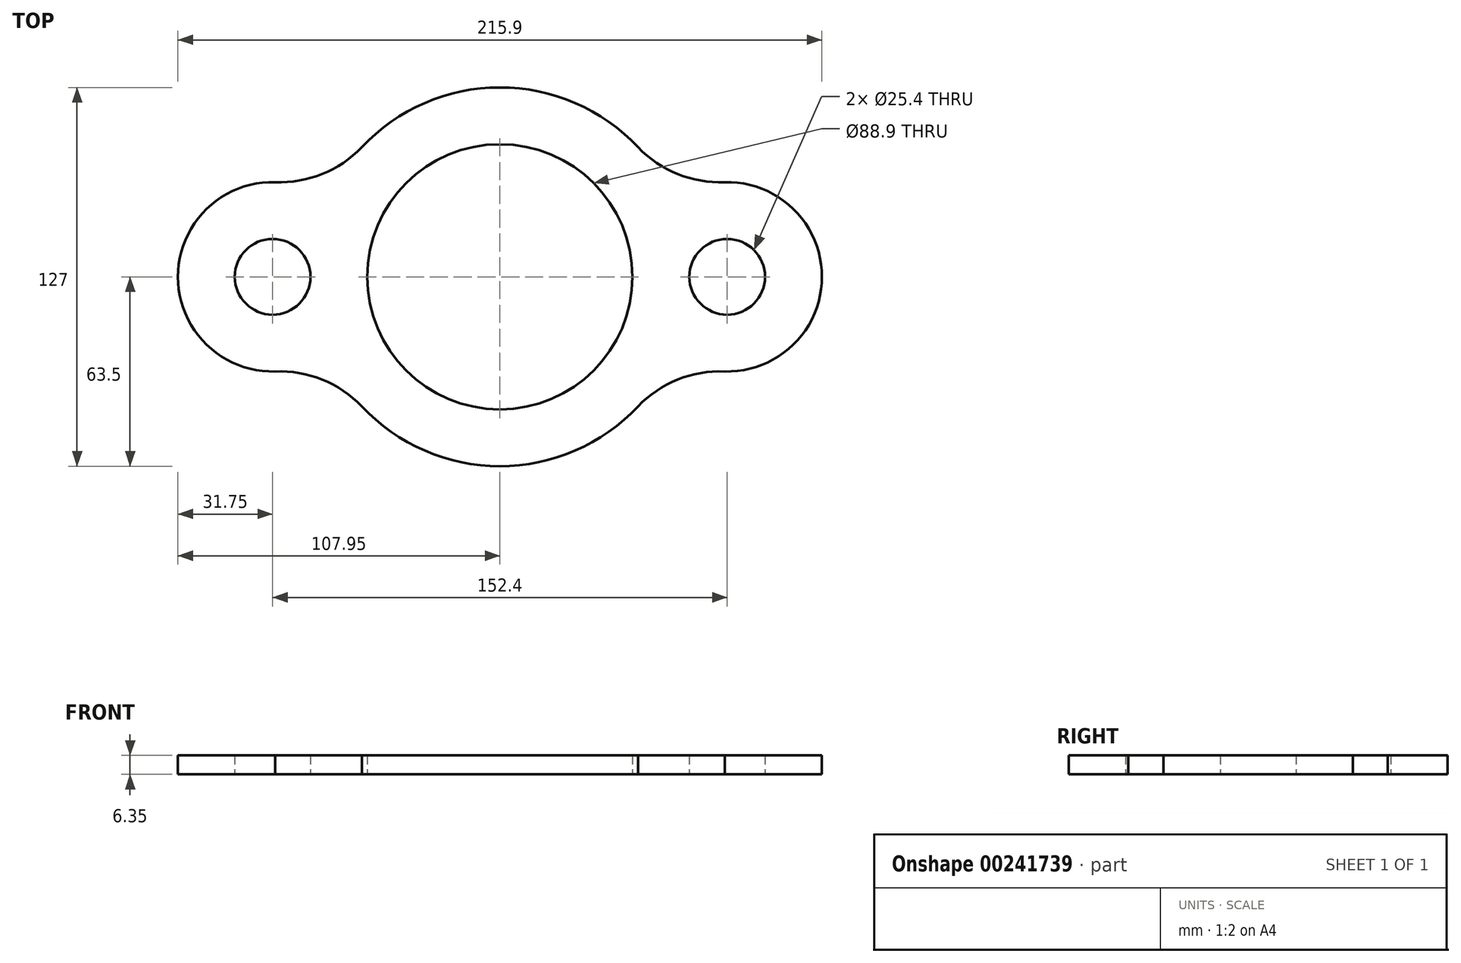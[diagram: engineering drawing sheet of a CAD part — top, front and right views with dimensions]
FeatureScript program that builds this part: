
annotation { "Feature Type Name" : "Feature", "Feature Type Description" : "" }
export const myFeature = defineFeature(function(context is Context, id is Id, definition is map)
    precondition{}
    {
        {
            var Q0;
            Q0=qCreatedBy(makeId("Top.planeOp"),FACE);
            var sketch = newSketch(context, id + "F0", { "sketchPlane" : qUnion([Q0])});
            skCircle(sketch, "E0", {"center": v(0, 0) * mm, "radius": 63.5 * mm});
            skCircle(sketch, "E1", {"center": v(-76.2, 0) * mm, "radius": 31.75 * mm});
            skCircle(sketch, "E2.MirrorC", {"center": v(76.2, 0) * mm, "radius": 31.75 * mm});
            skCircle(sketch, "E3", {"center": v(0, 0) * mm, "radius": 44.45 * mm});
            skCircle(sketch, "E4", {"center": v(-76.2, 0) * mm, "radius": 12.7 * mm});
            skCircle(sketch, "E5", {"center": v(76.2, 0) * mm, "radius": 12.7 * mm});
            skArc(sketch, "E6", {"start": v(75.35, -31.74) * mm, "mid": v(59.57, -34.47) * mm, "end": v(46.3, -43.45) * mm});
            skArc(sketch, "E7.MirrorCS", {"start": v(-75.35, -31.74) * mm, "mid": v(-59.57, -34.47) * mm, "end": v(-46.3, -43.45) * mm});
            skArc(sketch, "E8.MirrorCS", {"start": v(-75.35, 31.74) * mm, "mid": v(-59.57, 34.47) * mm, "end": v(-46.3, 43.45) * mm});
            skArc(sketch, "E9.MirrorCS", {"start": v(75.35, 31.74) * mm, "mid": v(59.57, 34.47) * mm, "end": v(46.3, 43.45) * mm});
            skSolve(sketch);
        }
        {
            var Q0;
            {var subQ0=sQuery(id+"F0.wireOp",EDGE,"E8.MirrorCS");var subQ1=sQuery(id+"F0.wireOp",EDGE,"E0");var subQ2=makeQuery(id+"F0.imprint","INTERSECT",VERTEX,{"derivedFrom":[subQ1,subQ0]});Q0=makeQuery(id+"F0.imprint","IMPRINT",FACE,{"disambiguationData":[TD([[makeQuery(id+"F0.imprint","IMPRINT",EDGE,{"disambiguationData":[TD([[subQ2,-1.0]])],"derivedFrom":subQ1}),-1.0]])]});}
            var Q1;
            {var subQ0=sQuery(id+"F0.wireOp",EDGE,"E0");var subQ1=makeQuery(id+"F0.imprint","INTERSECT",VERTEX,{"derivedFrom":[subQ0,sQuery(id+"F0.wireOp",EDGE,"E4")]});Q1=makeQuery(id+"F0.imprint","IMPRINT",FACE,{"disambiguationData":[TD([[makeQuery(id+"F0.imprint","IMPRINT",EDGE,{"disambiguationData":[TD([[subQ1,1.0]])],"derivedFrom":subQ0}),1.0]])]});}
            var Q2;
            {var subQ4=sQuery(id+"F0.wireOp",EDGE,"E4");Q2=makeQuery(id+"F0.imprint","IMPRINT",FACE,{"disambiguationData":[TD([[makeQuery(id+"F0.imprint","IMPRINT",EDGE,{"derivedFrom":subQ4}),-1.0]])]});}
            var Q3;
            {var subQ5=sQuery(id+"F0.wireOp",EDGE,"E0");var subQ8=makeQuery(id+"F0.imprint","INTERSECT",VERTEX,{"derivedFrom":[subQ5,sQuery(id+"F0.wireOp",EDGE,"E7.MirrorCS")]});Q3=makeQuery(id+"F0.imprint","IMPRINT",FACE,{"disambiguationData":[TD([[makeQuery(id+"F0.imprint","IMPRINT",EDGE,{"disambiguationData":[TD([[subQ8,1.0]])],"derivedFrom":subQ5}),1.0]])]});}
            var Q4;
            {var subQ0=sQuery(id+"F0.wireOp",EDGE,"E7.MirrorCS");var subQ1=sQuery(id+"F0.wireOp",EDGE,"E0");var subQ2=makeQuery(id+"F0.imprint","INTERSECT",VERTEX,{"derivedFrom":[subQ1,subQ0]});Q4=makeQuery(id+"F0.imprint","IMPRINT",FACE,{"disambiguationData":[TD([[makeQuery(id+"F0.imprint","IMPRINT",EDGE,{"disambiguationData":[TD([[subQ2,1.0]])],"derivedFrom":subQ1}),-1.0]])]});}
            var Q5;
            {var subQ5=sQuery(id+"F0.wireOp",EDGE,"E0");var subQ8=makeQuery(id+"F0.imprint","INTERSECT",VERTEX,{"derivedFrom":[subQ5,sQuery(id+"F0.wireOp",EDGE,"E9.MirrorCS")]});Q5=makeQuery(id+"F0.imprint","IMPRINT",FACE,{"disambiguationData":[TD([[makeQuery(id+"F0.imprint","IMPRINT",EDGE,{"disambiguationData":[TD([[subQ8,1.0]])],"derivedFrom":subQ5}),1.0]])]});}
            var Q6;
            {var subQ0=sQuery(id+"F0.wireOp",EDGE,"E0");var subQ1=makeQuery(id+"F0.imprint","INTERSECT",VERTEX,{"derivedFrom":[subQ0,sQuery(id+"F0.wireOp",EDGE,"E5")]});Q6=makeQuery(id+"F0.imprint","IMPRINT",FACE,{"disambiguationData":[TD([[makeQuery(id+"F0.imprint","IMPRINT",EDGE,{"disambiguationData":[TD([[subQ1,-1.0]])],"derivedFrom":subQ0}),1.0]])]});}
            var Q7;
            {var subQ4=sQuery(id+"F0.wireOp",EDGE,"E5");Q7=makeQuery(id+"F0.imprint","IMPRINT",FACE,{"disambiguationData":[TD([[makeQuery(id+"F0.imprint","IMPRINT",EDGE,{"derivedFrom":subQ4}),-1.0]])]});}
            var Q8;
            {var subQ0=sQuery(id+"F0.wireOp",EDGE,"E9.MirrorCS");var subQ1=sQuery(id+"F0.wireOp",EDGE,"E0");var subQ2=makeQuery(id+"F0.imprint","INTERSECT",VERTEX,{"derivedFrom":[subQ1,subQ0]});Q8=makeQuery(id+"F0.imprint","IMPRINT",FACE,{"disambiguationData":[TD([[makeQuery(id+"F0.imprint","IMPRINT",EDGE,{"disambiguationData":[TD([[subQ2,1.0]])],"derivedFrom":subQ1}),-1.0]])]});}
            var Q9;
            {var subQ0=sQuery(id+"F0.wireOp",EDGE,"E6");var subQ1=sQuery(id+"F0.wireOp",EDGE,"E0");var subQ2=makeQuery(id+"F0.imprint","INTERSECT",VERTEX,{"derivedFrom":[subQ1,subQ0]});Q9=makeQuery(id+"F0.imprint","IMPRINT",FACE,{"disambiguationData":[TD([[makeQuery(id+"F0.imprint","IMPRINT",EDGE,{"disambiguationData":[TD([[subQ2,-1.0]])],"derivedFrom":subQ1}),-1.0]])]});}
            extrude(context, id + "F1", {"entities" : qUnion([Q0, Q1, Q2, Q3, Q4, Q5, Q6, Q7, Q8, Q9]), "depth" : 6.35 * mm});
        }
    });
